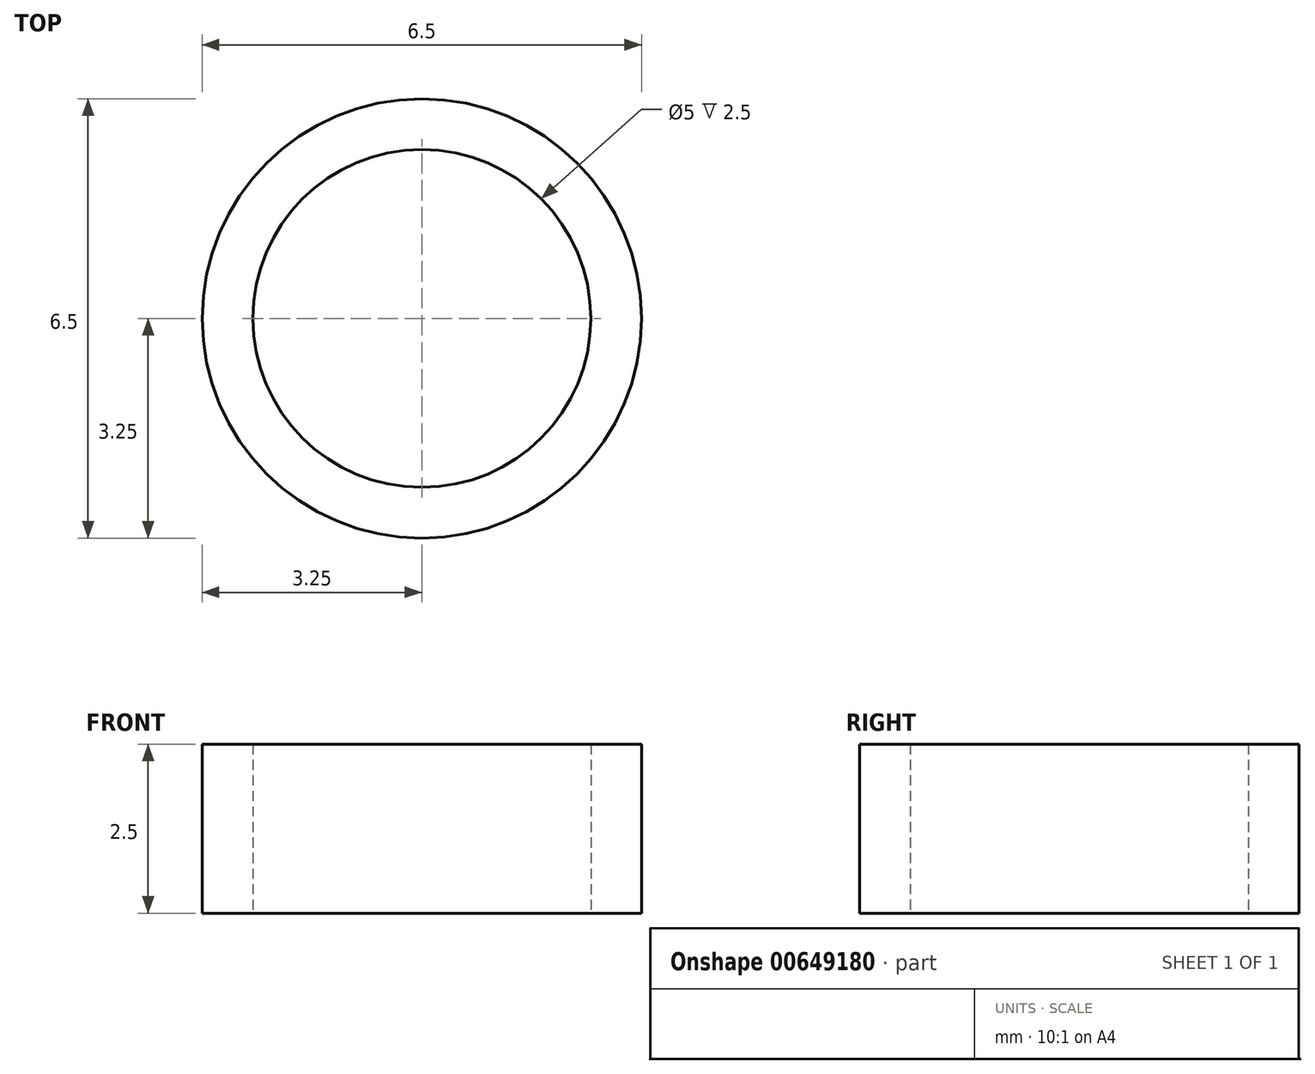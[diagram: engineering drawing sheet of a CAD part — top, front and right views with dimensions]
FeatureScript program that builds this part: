
annotation { "Feature Type Name" : "Feature", "Feature Type Description" : "" }
export const myFeature = defineFeature(function(context is Context, id is Id, definition is map)
    precondition{}
    {
        {
            var Q0;
            Q0=qCreatedBy(makeId("Top.planeOp"),FACE);
            var sketch = newSketch(context, id + "F0", { "sketchPlane" : qUnion([Q0])});
            skCircle(sketch, "E0", {"center": v(0, 0) * mm, "radius": 2.5 * mm});
            skCircle(sketch, "E1.0", {"center": v(0, 0) * mm, "radius": 3.25 * mm});
            skSolve(sketch);
        }
        {
            var Q0;
            Q0=qSketchRegion(id+"F0",true);
            extrude(context, id + "F1", {"entities" : qUnion([Q0]), "depth" : 2.5 * mm});
        }
    });
